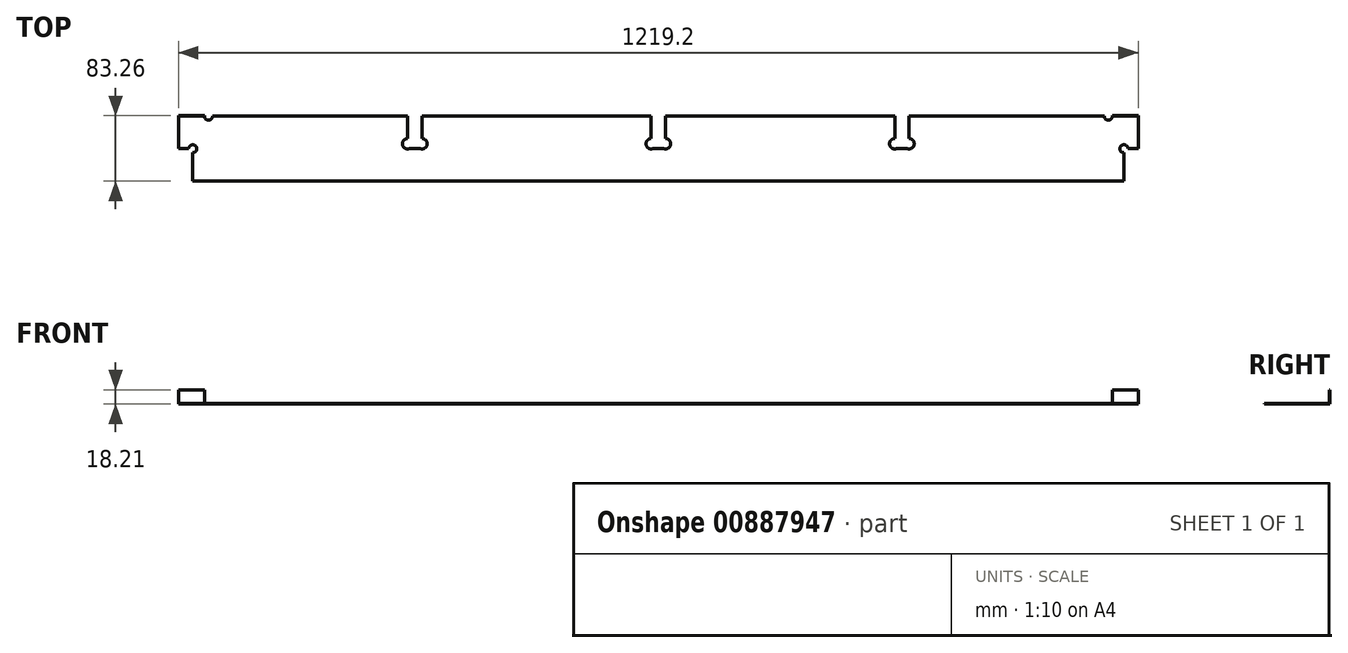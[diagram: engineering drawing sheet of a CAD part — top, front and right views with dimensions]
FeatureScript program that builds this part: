
annotation { "Feature Type Name" : "Feature", "Feature Type Description" : "" }
export const myFeature = defineFeature(function(context is Context, id is Id, definition is map)
    precondition{}
    {
        {
            assignVariable(context, id + "F0", {"name" : "WoodThickness", "anyValue" : .717});
        }
        {
            var Q0;
            Q0=qCreatedBy(makeId("Top.planeOp"),FACE);
            var sketch = newSketch(context, id + "F1", { "sketchPlane" : qUnion([Q0])});
            skLineSegment(sketch, "E0.bottom", {"start": v(609.6, 41.28) * mm, "end": v(-609.6, 41.28) * mm});
            skLineSegment(sketch, "E0.top", {"start": v(609.6, -41.28) * mm, "end": v(-609.6, -41.28) * mm});
            skLineSegment(sketch, "E0.left", {"start": v(609.6, 41.28) * mm, "end": v(609.6, -41.28) * mm});
            skLineSegment(sketch, "E0.right", {"start": v(-609.6, 41.28) * mm, "end": v(-609.6, -41.28) * mm});
            skPoint(sketch, "E0.middle", {"position": v(0, 0) * mm});
            skSolve(sketch);
        }
        {
            var Q0;
            Q0 = qSketchRegion(id + "F1", true);
            extrude(context, id + "F2", {"entities" : qUnion([Q0]), "depth" : (getVariable(context, 'WoodThickness')) * mm, "offsetDistance" : 25.4 * mm});
        }
        {
            var Q0;
            Q0=makeQuery(id+"F2.opExtrude","CAP_FACE",FACE,{"disambiguationData":[OSD([sQuery(id+"F1.wireOp",EDGE,"E0.bottom"),sQuery(id+"F1.wireOp",EDGE,"E0.top"),sQuery(id+"F1.wireOp",EDGE,"E0.left"),sQuery(id+"F1.wireOp",EDGE,"E0.right")])],"isStart":false});
            var sketch = newSketch(context, id + "F3", { "sketchPlane" : qUnion([Q0])});
            skLineSegment(sketch, "E1.bottom", {"start": v(-609.6, -41.28) * mm, "end": v(-591.39, -41.28) * mm});
            skLineSegment(sketch, "E1.top", {"start": v(-609.6, 0) * mm, "end": v(-591.39, 0) * mm});
            skLineSegment(sketch, "E1.left", {"start": v(-609.6, -41.28) * mm, "end": v(-609.6, 0) * mm});
            skLineSegment(sketch, "E1.right", {"start": v(-591.39, -41.28) * mm, "end": v(-591.39, 0) * mm});
            skLineSegment(sketch, "E2", {"start": v(0, 41.28) * mm, "end": v(0, -41.28) * mm, "construction": true});
            skLineSegment(sketch, "E3.MirrorCS", {"start": v(609.6, 0) * mm, "end": v(591.39, 0) * mm});
            skLineSegment(sketch, "E4.MirrorCS", {"start": v(591.39, -41.27) * mm, "end": v(591.39, 0) * mm});
            skArc(sketch, "E5", {"start": v(-591.39, -5.08) * mm, "mid": v(-587.8, 3.6) * mm, "end": v(-596.47, 0) * mm});
            skArc(sketch, "E6", {"start": v(591.39, -5.08) * mm, "mid": v(587.8, 3.6) * mm, "end": v(596.47, 0) * mm});
            skSolve(sketch);
        }
        {
            var Q0;
            Q0 = qSketchRegion(id + "F3", true);
            var Q1;
            {var subQ6=sQuery(id+"F3.wireOp",EDGE,"E3.MirrorCS");Q1=makeQuery(id+"F3.imprint","IMPRINT",FACE,{"disambiguationData":[TD([[makeQuery(id+"F3.imprint","IMPRINT",EDGE,{"derivedFrom":subQ6}),1.0]])]});}
            extrude(context, id + "F4", {"entities" : qUnion([Q0, Q1]), "operationType" : NewBodyOperationType.REMOVE, "endBound" : BoundingType.THROUGH_ALL, "oppositeDirection" : true, "depth" : 25.4 * mm, "offsetDistance" : 25.4 * mm});
        }
        {
            var Q0;
            Q0=makeQuery(id+"F2.opExtrude","CAP_FACE",FACE,{"disambiguationData":[OSD([sQuery(id+"F1.wireOp",EDGE,"E0.bottom"),sQuery(id+"F1.wireOp",EDGE,"E0.top"),sQuery(id+"F1.wireOp",EDGE,"E0.left"),sQuery(id+"F1.wireOp",EDGE,"E0.right")])],"isStart":false});
            var sketch = newSketch(context, id + "F5", { "sketchPlane" : qUnion([Q0])});
            skLineSegment(sketch, "E7.bottom", {"start": v(-318.46, 41.28) * mm, "end": v(-300.25, 41.28) * mm});
            skLineSegment(sketch, "E7.top", {"start": v(-318.46, 0) * mm, "end": v(-300.25, 0) * mm});
            skLineSegment(sketch, "E7.left", {"start": v(-318.46, 41.28) * mm, "end": v(-318.46, 0) * mm});
            skLineSegment(sketch, "E7.right", {"start": v(-300.25, 41.28) * mm, "end": v(-300.25, 0) * mm});
            skLineSegment(sketch, "E8.bottom", {"start": v(300.25, 41.28) * mm, "end": v(318.46, 41.28) * mm});
            skLineSegment(sketch, "E8.top", {"start": v(300.25, 0) * mm, "end": v(318.46, 0) * mm});
            skLineSegment(sketch, "E8.left", {"start": v(300.25, 41.28) * mm, "end": v(300.25, 0) * mm});
            skLineSegment(sketch, "E8.right", {"start": v(318.46, 41.28) * mm, "end": v(318.46, 0) * mm});
            skLineSegment(sketch, "E9", {"start": v(-609.6, 0) * mm, "end": v(-318.46, 0) * mm, "construction": true});
            skLineSegment(sketch, "E10", {"start": v(318.46, 0) * mm, "end": v(609.6, 0) * mm, "construction": true});
            skLineSegment(sketch, "E11.bottom", {"start": v(-9.1, 41.28) * mm, "end": v(9.1, 41.28) * mm});
            skLineSegment(sketch, "E11.top", {"start": v(-9.1, 0) * mm, "end": v(9.1, 0) * mm});
            skLineSegment(sketch, "E11.left", {"start": v(-9.1, 41.28) * mm, "end": v(-9.1, 0) * mm});
            skLineSegment(sketch, "E11.right", {"start": v(9.1, 41.28) * mm, "end": v(9.1, 0) * mm});
            skLineSegment(sketch, "E12", {"start": v(-300.25, 0) * mm, "end": v(-9.1, 0) * mm, "construction": true});
            skLineSegment(sketch, "E13", {"start": v(9.1, 0) * mm, "end": v(300.25, 0) * mm, "construction": true});
            skLineSegment(sketch, "E14", {"start": v(-318.46, 6.35) * mm, "end": v(318.46, 6.35) * mm, "construction": true});
            skArc(sketch, "E15", {"start": v(300.25, 12.95) * mm, "mid": v(293.7, 5.43) * mm, "end": v(302.06, 0) * mm});
            skArc(sketch, "E16", {"start": v(318.46, 12.95) * mm, "mid": v(325, 5.43) * mm, "end": v(316.64, 0) * mm});
            skArc(sketch, "E17", {"start": v(9.1, 12.95) * mm, "mid": v(15.65, 5.43) * mm, "end": v(7.3, 0) * mm});
            skArc(sketch, "E18", {"start": v(-9.1, 12.95) * mm, "mid": v(-15.65, 5.43) * mm, "end": v(-7.3, 0) * mm});
            skArc(sketch, "E19", {"start": v(-300.25, 12.95) * mm, "mid": v(-293.7, 5.43) * mm, "end": v(-302.06, 0) * mm});
            skArc(sketch, "E20", {"start": v(-318.46, 12.95) * mm, "mid": v(-325, 5.43) * mm, "end": v(-316.64, 0) * mm});
            skSolve(sketch);
        }
        {
            var Q0;
            Q0 = qSketchRegion(id + "F5", true);
            extrude(context, id + "F6", {"entities" : qUnion([Q0]), "operationType" : NewBodyOperationType.REMOVE, "endBound" : BoundingType.THROUGH_ALL, "oppositeDirection" : true, "depth" : 25.4 * mm, "offsetDistance" : 25.4 * mm});
        }
        {
            var Q0;
            {var subQ0=sQuery(id+"F1.wireOp",EDGE,"E0.right");var subQ3=sQuery(id+"F1.wireOp",EDGE,"E0.bottom");Q0=makeQuery(id+"F6.boolean.opBoolean","SPLIT",FACE,{"disambiguationData":[TD([makeQuery(id+"F2.opExtrude","SWEPT_FACE",FACE,{"disambiguationData":[OSD([subQ0])]})])],"derivedFrom":makeQuery(id+"F2.opExtrude","SWEPT_FACE",FACE,{"disambiguationData":[OSD([subQ3])]})});}
            var sketch = newSketch(context, id + "F7", { "sketchPlane" : qUnion([Q0])});
            skLineSegment(sketch, "E21.bottom", {"start": v(609.6, 0) * mm, "end": v(571.5, 0) * mm});
            skLineSegment(sketch, "E21.top", {"start": v(609.6, 18.21) * mm, "end": v(571.5, 18.21) * mm});
            skLineSegment(sketch, "E21.left", {"start": v(609.6, 0) * mm, "end": v(609.6, 18.21) * mm});
            skLineSegment(sketch, "E21.right", {"start": v(571.5, 0) * mm, "end": v(571.5, 18.21) * mm});
            skLineSegment(sketch, "E22.bottom", {"start": v(-609.6, 18.21) * mm, "end": v(-571.5, 18.21) * mm});
            skLineSegment(sketch, "E22.top", {"start": v(-609.6, 0) * mm, "end": v(-571.5, 0) * mm});
            skLineSegment(sketch, "E22.left", {"start": v(-609.6, 18.21) * mm, "end": v(-609.6, 0) * mm});
            skLineSegment(sketch, "E22.right", {"start": v(-571.5, 18.21) * mm, "end": v(-571.5, 0) * mm});
            skSolve(sketch);
        }
        {
            var Q0;
            Q0 = qSketchRegion(id + "F7", true);
            extrude(context, id + "F8", {"entities" : qUnion([Q0]), "operationType" : NewBodyOperationType.ADD, "depth" : (getVariable(context, 'WoodThickness')) * mm, "offsetDistance" : 25.4 * mm});
        }
        {
            var Q0;
            Q0=makeQuery(id+"F8.boolean.opBoolean","MERGE",FACE,{"derivedFrom":[makeQuery(id+"F2.opExtrude","CAP_FACE",FACE,{"disambiguationData":[OSD([sQuery(id+"F1.wireOp",EDGE,"E0.bottom"),sQuery(id+"F1.wireOp",EDGE,"E0.top"),sQuery(id+"F1.wireOp",EDGE,"E0.left"),sQuery(id+"F1.wireOp",EDGE,"E0.right")])],"isStart":true}),makeQuery(id+"F8.opExtrude","SWEPT_FACE",FACE,{"disambiguationData":[OSD([sQuery(id+"F7.wireOp",EDGE,"E21.bottom")])]}),makeQuery(id+"F8.opExtrude","SWEPT_FACE",FACE,{"disambiguationData":[OSD([sQuery(id+"F7.wireOp",EDGE,"E22.top")])]})]});
            var sketch = newSketch(context, id + "F9", { "sketchPlane" : qUnion([Q0])});
            skCircle(sketch, "E23", {"center": v(571.5, -41.28) * mm, "radius": 5.08 * mm});
            skCircle(sketch, "E24", {"center": v(-571.5, -41.28) * mm, "radius": 5.08 * mm});
            skSolve(sketch);
        }
        {
            var Q0;
            Q0 = qSketchRegion(id + "F9", true);
            extrude(context, id + "F10", {"entities" : qUnion([Q0]), "operationType" : NewBodyOperationType.REMOVE, "endBound" : BoundingType.THROUGH_ALL, "oppositeDirection" : true, "depth" : 25.4 * mm, "offsetDistance" : 25.4 * mm});
        }
    });
